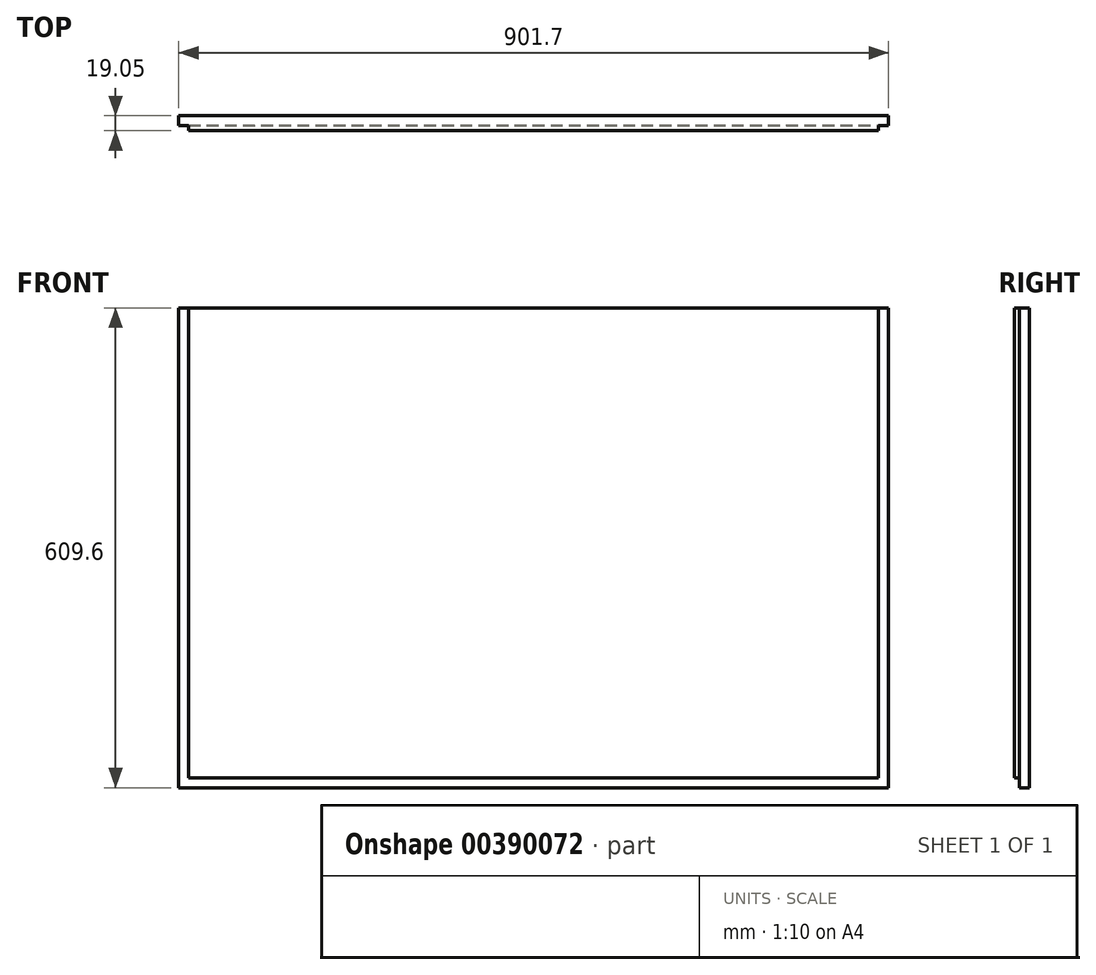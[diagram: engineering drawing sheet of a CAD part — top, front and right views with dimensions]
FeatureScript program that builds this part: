
annotation { "Feature Type Name" : "Feature", "Feature Type Description" : "" }
export const myFeature = defineFeature(function(context is Context, id is Id, definition is map)
    precondition{}
    {
        {
            var Q0;
            Q0=qCreatedBy(makeId("Front.planeOp"),FACE);
            var sketch = newSketch(context, id + "F0", { "sketchPlane" : qUnion([Q0])});
            skLineSegment(sketch, "E0.bottom", {"start": v(0, 0) * mm, "end": v(901.7, 0) * mm});
            skLineSegment(sketch, "E0.top", {"start": v(0, 609.6) * mm, "end": v(901.7, 609.6) * mm});
            skLineSegment(sketch, "E0.left", {"start": v(0, 0) * mm, "end": v(0, 609.6) * mm});
            skLineSegment(sketch, "E0.right", {"start": v(901.7, 0) * mm, "end": v(901.7, 609.6) * mm});
            skSolve(sketch);
        }
        {
            var Q0;
            Q0=makeQuery(id+"F0.imprint","IMPRINT",FACE,{"disambiguationData":[TD([[makeQuery(id+"F0.imprint","IMPRINT",EDGE,{"derivedFrom":sQuery(id+"F0.wireOp",EDGE,"E0.bottom")}),1.0]])]});
            extrude(context, id + "F1", {"entities" : qUnion([Q0]), "depth" : 19.05 * mm});
        }
        {
            var Q0;
            Q0=makeQuery(id+"F1.opExtrude","SWEPT_FACE",FACE,{"disambiguationData":[OSD([sQuery(id+"F0.wireOp",EDGE,"E0.top")])]});
            var sketch = newSketch(context, id + "F2", { "sketchPlane" : qUnion([Q0])});
            skLineSegment(sketch, "E1", {"start": v(0, -19.05) * mm, "end": v(12.7, -19.05) * mm});
            skLineSegment(sketch, "E2", {"start": v(12.7, -19.05) * mm, "end": v(12.7, -12.7) * mm});
            skLineSegment(sketch, "E3", {"start": v(12.7, -12.7) * mm, "end": v(0, -12.7) * mm});
            skLineSegment(sketch, "E4", {"start": v(0, -12.7) * mm, "end": v(0, -19.05) * mm});
            skLineSegment(sketch, "E5", {"start": v(901.7, -19.05) * mm, "end": v(889, -19.05) * mm});
            skLineSegment(sketch, "E6", {"start": v(889, -19.05) * mm, "end": v(889, -12.7) * mm});
            skLineSegment(sketch, "E7", {"start": v(889, -12.7) * mm, "end": v(901.7, -12.7) * mm});
            skLineSegment(sketch, "E8", {"start": v(901.7, -12.7) * mm, "end": v(901.7, -19.05) * mm});
            skSolve(sketch);
        }
        {
            var Q0;
            Q0=makeQuery(id+"F2.imprint","IMPRINT",FACE,{"disambiguationData":[TD([[makeQuery(id+"F2.imprint","IMPRINT",EDGE,{"derivedFrom":sQuery(id+"F2.wireOp",EDGE,"E5")}),1.0]])]});
            var Q1;
            Q1=makeQuery(id+"F2.imprint","IMPRINT",FACE,{"disambiguationData":[TD([[makeQuery(id+"F2.imprint","IMPRINT",EDGE,{"derivedFrom":sQuery(id+"F2.wireOp",EDGE,"E1")}),1.0]])]});
            extrude(context, id + "F3", {"entities" : qUnion([Q0, Q1]), "operationType" : NewBodyOperationType.REMOVE, "endBound" : BoundingType.THROUGH_ALL, "oppositeDirection" : true, "depth" : 25.4 * mm});
        }
        {
            var Q0;
            Q0=makeQuery(id+"F1.opExtrude","SWEPT_FACE",FACE,{"disambiguationData":[OSD([sQuery(id+"F0.wireOp",EDGE,"E0.right")])]});
            var sketch = newSketch(context, id + "F4", { "sketchPlane" : qUnion([Q0])});
            skLineSegment(sketch, "E9", {"start": v(0, 0) * mm, "end": v(-12.7, 0) * mm});
            skLineSegment(sketch, "E10", {"start": v(-12.7, 0) * mm, "end": v(-19.05, 0) * mm});
            skLineSegment(sketch, "E11", {"start": v(-19.05, 0) * mm, "end": v(-19.05, 12.7) * mm});
            skLineSegment(sketch, "E12", {"start": v(-19.05, 12.7) * mm, "end": v(-12.7, 12.7) * mm});
            skLineSegment(sketch, "E13", {"start": v(-12.7, 12.7) * mm, "end": v(-12.7, 0) * mm});
            skSolve(sketch);
        }
        {
            var Q0;
            Q0 = qSketchRegion(id + "F4", true);
            extrude(context, id + "F5", {"entities" : qUnion([Q0]), "operationType" : NewBodyOperationType.REMOVE, "endBound" : BoundingType.THROUGH_ALL, "oppositeDirection" : true, "depth" : 25.4 * mm});
        }
    });
